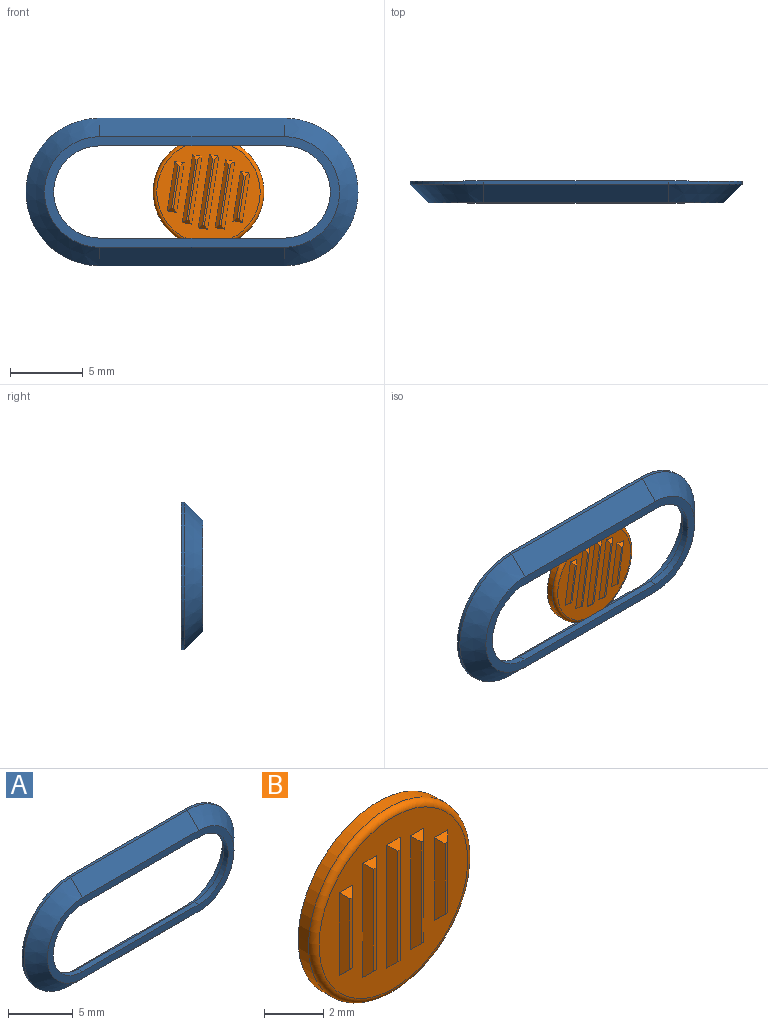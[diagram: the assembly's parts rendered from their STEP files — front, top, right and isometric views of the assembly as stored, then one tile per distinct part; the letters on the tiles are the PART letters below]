
ASSEMBLY  parts=2 mates=1
PART A: 19 faces, bbox 22.9x1.5x10.2 mm
  f0: plane 12.7x0.5mm, normal (0,0,-1), area 6.4mm2, adj f1,f3,f9,f14
  f1: cylinder r=3.17mm len=6.35mm, axis (0,1,0), area 5mm2, adj f0,f2,f9,f14
  f2: plane 12.7x0.5mm, normal (0,0,1), area 6.4mm2, adj f1,f3,f9,f14
  f3: cylinder r=3.17mm len=6.35mm, axis (0,1,0), area 5mm2, adj f0,f2,f9,f14
  f4: plane 22.86x10.16mm, normal (0,1,0), area 55mm2, adj f5,f6,f7,f8,f10,f11,f12,f13
  f5: cylinder r=5.08mm len=10.16mm, axis (0,1,0), area 3.7mm2, adj f4,f6,f8,f18
  f6: plane 12.7x0.23mm, normal (0,0,1), area 2.9mm2, adj f4,f5,f7,f17
  f7: cylinder r=5.08mm len=10.16mm, axis (0,1,0), area 3.7mm2, adj f4,f6,f8,f15
  f8: plane 12.7x0.23mm, normal (0,0,-1), area 2.9mm2, adj f4,f5,f7,f16
  f9: plane 20.32x7.62mm, normal (0,-1,0), area 30.1mm2, adj f0,f1,f2,f3,f15,f16,f17,f18
  f10: cylinder r=4.06mm len=8.13mm, axis (0,1,0), area 12.8mm2, adj f4,f11,f13,f14
  f11: plane 12.7x1mm, normal (0,0,-1), area 12.7mm2, adj f4,f10,f12,f14
  f12: cylinder r=4.06mm len=8.13mm, axis (0,1,0), area 12.8mm2, adj f4,f11,f13,f14
  f13: plane 12.7x1mm, normal (0,0,1), area 12.7mm2, adj f4,f10,f12,f14
  f14: plane 20.83x8.13mm, normal (0,1,0), area 42.8mm2, adj f0,f1,f2,f3,f10,f11,f12,f13
  f15: cone r=3.81mm half-angle=45deg, axis (0,1,0), area 25.1mm2, adj f7,f9,f16,f17
  f16: plane 12.7x1.27mm, normal (0,-0.71,-0.71), area 22.8mm2, adj f8,f9,f15,f18
  f17: plane 12.7x1.27mm, normal (0,-0.71,0.71), area 22.8mm2, adj f6,f9,f15,f18
  f18: cone r=3.81mm half-angle=45deg, axis (0,1,0), area 25.1mm2, adj f5,f9,f16,f17
PART B: 29 faces, bbox 8.2x1x8.2 mm
  f0: cylinder r=3.81mm len=7.62mm, axis (0,1,0), area 11.9mm2, adj f2,f3
  f1: plane 7.11x7.11mm, normal (0,-1,0), area 26.1mm2, adj f3,f9,f10,f11,f12,f13,f14,f15
  f2: plane 7.62x7.62mm, normal (0,1,0), area 45.6mm2, adj f0
  f3: torus R=3.56mm, axis (0,-1,0), area 9.3mm2, adj f0,f1
  f4: plane 4.21x0.13mm, normal (0,-1,0), area 0.5mm2, adj f21,f22,f23,f24
  f5: plane 2.93x0.13mm, normal (0,-1,0), area 0.4mm2, adj f25,f26,f27,f28
  f6: plane 4.59x0.13mm, normal (0,-1,0), area 0.6mm2, adj f17,f18,f19,f20
  f7: plane 4.21x0.13mm, normal (0,-1,0), area 0.5mm2, adj f13,f14,f15,f16
  f8: plane 2.93x0.13mm, normal (0,-1,0), area 0.4mm2, adj f9,f10,f11,f12
  f9: plane 3.44x0.25mm, normal (-0.71,-0.71,0), area 1.1mm2, adj f1,f8,f10,f11
  f10: plane 0.64x0.25mm, normal (0,-0.71,0.71), area 0.1mm2, adj f1,f8,f9,f12
  f11: plane 0.64x0.25mm, normal (0,-0.71,-0.71), area 0.1mm2, adj f1,f8,f9,f12
  f12: plane 3.44x0.25mm, normal (0.71,-0.71,0), area 1.1mm2, adj f1,f8,f10,f11
  f13: plane 4.72x0.25mm, normal (-0.71,-0.71,0), area 1.6mm2, adj f1,f7,f14,f15
  f14: plane 0.64x0.25mm, normal (0,-0.71,0.71), area 0.1mm2, adj f1,f7,f13,f16
  f15: plane 0.64x0.25mm, normal (0,-0.71,-0.71), area 0.1mm2, adj f1,f7,f13,f16
  f16: plane 4.72x0.25mm, normal (0.71,-0.71,0), area 1.6mm2, adj f1,f7,f14,f15
  f17: plane 5.1x0.25mm, normal (-0.71,-0.71,0), area 1.7mm2, adj f1,f6,f18,f19
  f18: plane 0.64x0.25mm, normal (0,-0.71,0.71), area 0.1mm2, adj f1,f6,f17,f20
  f19: plane 0.64x0.25mm, normal (0,-0.71,-0.71), area 0.1mm2, adj f1,f6,f17,f20
  f20: plane 5.1x0.25mm, normal (0.71,-0.71,0), area 1.7mm2, adj f1,f6,f18,f19
  f21: plane 4.72x0.25mm, normal (-0.71,-0.71,0), area 1.6mm2, adj f1,f4,f22,f23
  f22: plane 0.64x0.25mm, normal (0,-0.71,0.71), area 0.1mm2, adj f1,f4,f21,f24
  f23: plane 0.64x0.25mm, normal (0,-0.71,-0.71), area 0.1mm2, adj f1,f4,f21,f24
  f24: plane 4.72x0.25mm, normal (0.71,-0.71,0), area 1.6mm2, adj f1,f4,f22,f23
  f25: plane 3.44x0.25mm, normal (0.71,-0.71,0), area 1.1mm2, adj f1,f5,f26,f27
  f26: plane 0.64x0.25mm, normal (0,-0.71,0.71), area 0.1mm2, adj f1,f5,f25,f28
  f27: plane 0.64x0.25mm, normal (0,-0.71,-0.71), area 0.1mm2, adj f1,f5,f25,f28
  f28: plane 3.44x0.25mm, normal (-0.71,-0.71,0), area 1.1mm2, adj f1,f5,f26,f27
PLACE A t=(0.38,0.78,0.77)mm fixed
PLACE B rot(axis=(0,1,0),8.7deg) t=(1.52,0.78,0.77)mm
MATE pin_slot B.f0 <-> A.f4  axis (0,1,0) through (1.52,0.78,0.77)mm
